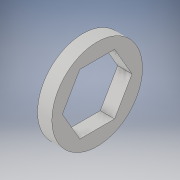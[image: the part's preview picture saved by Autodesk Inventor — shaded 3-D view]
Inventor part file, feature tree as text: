
AUTODESK INVENTOR PART (.ipt)
format: ipt  version: 2018 (Build 220112000, 112)  size: 103,936 bytes
history: native  units: in
note: dims shown in document units (in); Inventor stores cm internally (conversion verified against a paired STEP export)
features: extrude x1, sketch x1
ambient origin geometry x8: Origin, YZ Plane, XZ Plane, XY Plane, X Axis, Y Axis, Z Axis, Center Point
bodies: Solid1 (feature_tree)
feature tree (2):
  extrude  "Extrusion1"  Depth=0.119in TaperAngle=0.0deg
  sketch  "Sketch1"  dims[d0=0.75in d3=0.119in d4=0.0in]
